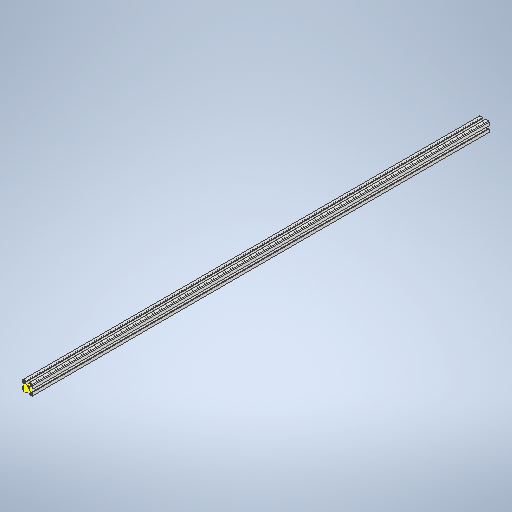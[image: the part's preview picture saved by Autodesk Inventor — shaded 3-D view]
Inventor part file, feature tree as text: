
AUTODESK INVENTOR PART (.ipt)
format: ipt  version: 2025 (Build 290162000, 162)  size: 314,368 bytes
history: native  units: in
note: dims shown in document units (in); Inventor stores cm internally (conversion verified against a paired STEP export)
features: sketch x2, extrude x1
ambient origin geometry x8: Origin, YZ Plane, XZ Plane, XY Plane, X Axis, Y Axis, Z Axis, Center Point
bodies: Solid1 (feature_tree)
feature tree (3):
  extrude  "Extrusion1"  Depth=53.1496in
  sketch  "Sketch2"  dims[d9=0.0344in]
  sketch  "Sketch1"  dims[d6=53.1496in d7=0.0in d8=0.1969in]
